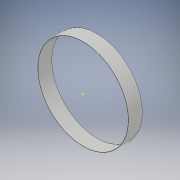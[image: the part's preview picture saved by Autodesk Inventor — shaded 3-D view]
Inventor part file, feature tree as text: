
AUTODESK INVENTOR PART (.ipt)
format: ipt  version: 2019 (Build 230136000, 136)  size: 105,984 bytes
history: native  units: mm
features: sketch x3, extrude x2
ambient origin geometry x8: Origin, YZ Plane, XZ Plane, XY Plane, X Axis, Y Axis, Z Axis, Center Point
bodies: Solid1 (feature_tree)
feature tree (5):
  extrude  "Extrusion1"  Depth=9.555mm TaperAngle=0.0deg
  sketch  "Sketch2"  dims[d3=62.6mm d4=9.555mm d5=0.0mm]
  extrude  "Extrusion2"  Depth=9.555mm TaperAngle=0.0deg
  sketch  "Sketch1"  dims[d0=62.9mm d1=9.555mm d2=0.0mm]
  sketch  "Sketch3"
